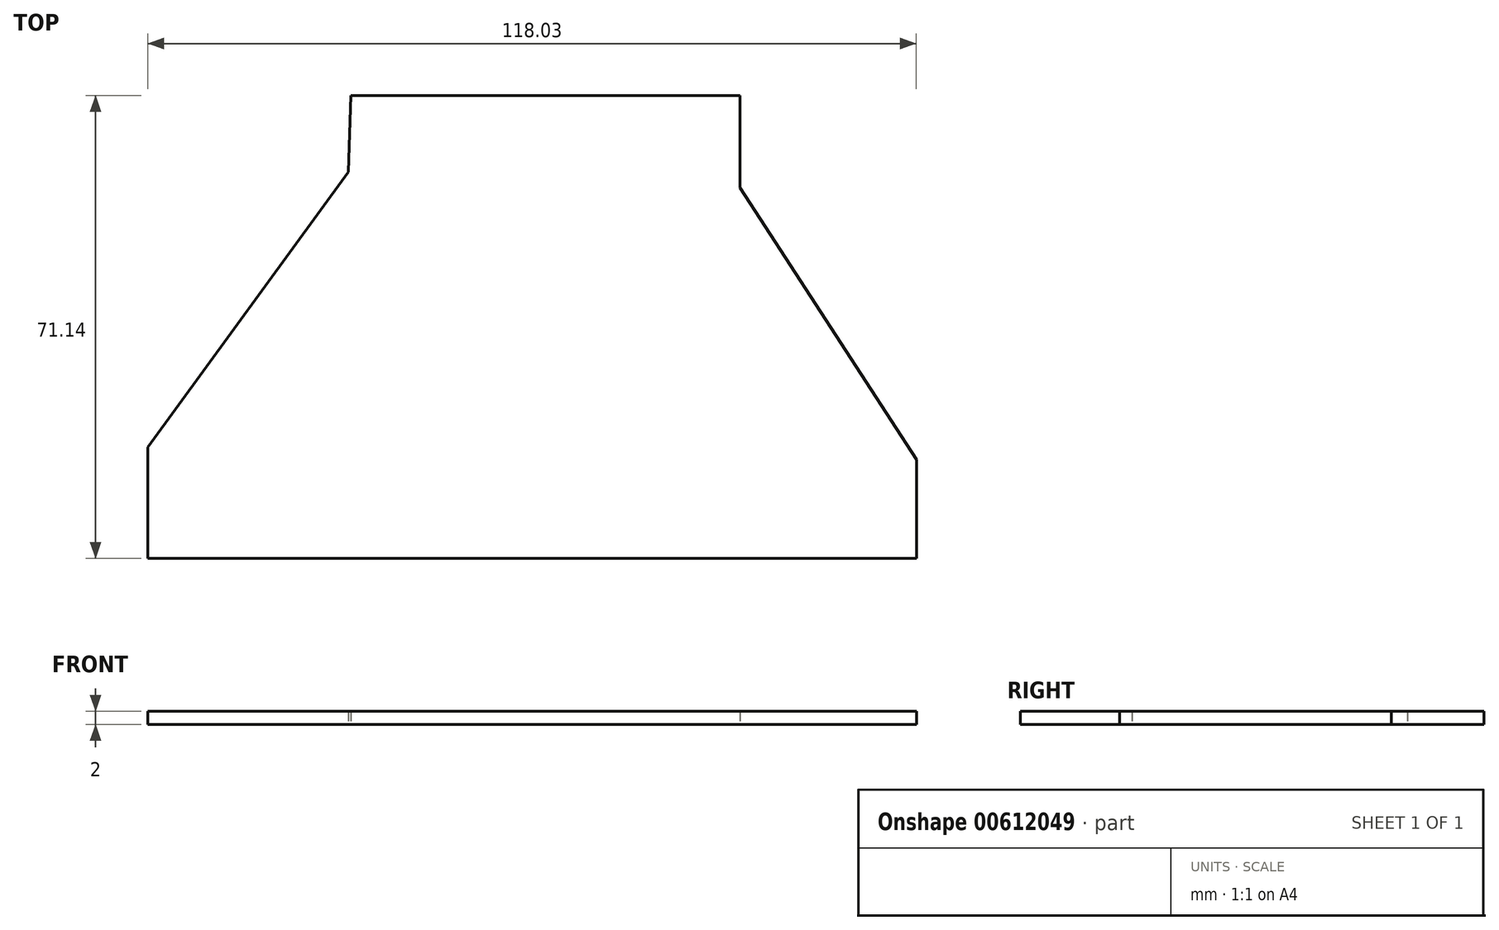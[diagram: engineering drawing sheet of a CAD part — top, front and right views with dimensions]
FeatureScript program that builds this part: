
annotation { "Feature Type Name" : "Feature", "Feature Type Description" : "" }
export const myFeature = defineFeature(function(context is Context, id is Id, definition is map)
    precondition{}
    {
        {
            var Q0;
            Q0=qCreatedBy(makeId("Top.planeOp"),FACE);
            var sketch = newSketch(context, id + "F0", { "sketchPlane" : qUnion([Q0])});
            skLineSegment(sketch, "E0", {"start": v(-26.22, 0) * mm, "end": v(33.55, 0) * mm});
            skLineSegment(sketch, "E1", {"start": v(33.55, 0) * mm, "end": v(33.55, -14.2) * mm});
            skLineSegment(sketch, "E2", {"start": v(33.55, -14.2) * mm, "end": v(60.61, -55.91) * mm});
            skLineSegment(sketch, "E3", {"start": v(60.61, -55.91) * mm, "end": v(60.61, -71.14) * mm});
            skLineSegment(sketch, "E4", {"start": v(60.61, -71.14) * mm, "end": v(-57.42, -71.14) * mm});
            skLineSegment(sketch, "E5", {"start": v(-57.42, -71.14) * mm, "end": v(-57.42, -54.03) * mm});
            skLineSegment(sketch, "E6", {"start": v(-57.42, -54.03) * mm, "end": v(-26.6, -11.75) * mm});
            skLineSegment(sketch, "E7", {"start": v(-26.6, -11.75) * mm, "end": v(-26.22, 0) * mm});
            skSolve(sketch);
        }
        {
            var Q0;
            Q0=makeQuery(id+"F0.imprint","IMPRINT",FACE,{"disambiguationData":[TD([[makeQuery(id+"F0.imprint","IMPRINT",EDGE,{"derivedFrom":sQuery(id+"F0.wireOp",EDGE,"E0")}),-1.0]])]});
            extrude(context, id + "F1", {"entities" : qUnion([Q0]), "depth" : 2 * mm, "offsetDistance" : 25 * mm});
        }
    });
